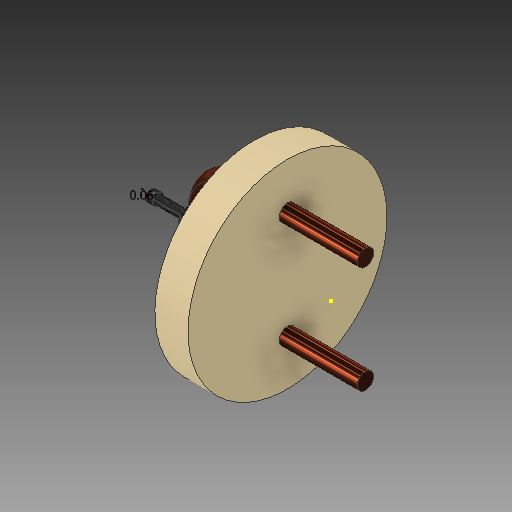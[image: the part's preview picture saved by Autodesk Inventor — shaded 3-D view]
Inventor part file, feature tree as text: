
AUTODESK INVENTOR PART (.ipt)
format: ipt  version: 2017.3 (Build 213256000, 256)  size: 282,112 bytes
history: native  units: mm
features: sketch x23, extrude x12, plane x8, other x6, sweep x2, move_body x1, loft x1
ambient origin geometry x8: Origin, YZ Plane, XZ Plane, XY Plane, X Axis, Y Axis, Z Axis, Center Point
bodies: Solid1 (feature_tree)
feature tree (53):
  extrude  "Extrusion1"  Depth=2.0mm TaperAngle=0.0deg
  sketch  "Sketch2"  dims[d3=1.0mm d4=7.45mm]
  move_body  "Move Body1"
  extrude  "Extrusion2"  Depth=1.0mm
  plane  "Work Plane2"
  sketch  "Sketch3"  dims[d5=1.0mm d6=1.0mm]
  sketch  "Sketch4"  dims[d7=-4.7mm d8=0.0mm d9=0.0mm d10=7.7mm d11=0.0mm]
  sketch  "Sketch5"  dims[d13=3.5mm d14=1.0mm]
  sweep  "Sweep1"
  sketch  "Sketch7"  dims[d21=90.0deg d22=0.5mm d23=-0.5mm d24=0.2mm d25=0.0mm]
  sketch  "Sketch8"  dims[d26=0.1mm d27=0.0mm d28=0.2mm d29=0.0mm]
  sketch  "Sketch9"  dims[d30=0.1mm d31=0.0mm d33=0.25mm]
  plane  "Work Plane3"
  sweep  "Sweep2"
  other  "Work Axis1"
  other  "Work Point1"
  other  "Work Point2"
  other  "Work Point3"
  plane  "Work Plane4"
  plane  "Work Plane5"
  plane  "Work Plane6"
  extrude  "Extrusion3"  Depth=1.0mm
  extrude  "Extrusion4"  TaperAngle=0.0deg  [1 undecoded]
  extrude  "Extrusion5"  Depth=0.2mm TaperAngle=0.0deg
  extrude  "Extrusion6"  Depth=0.2mm TaperAngle=0.0deg
  sketch  "Sketch14"  dims[d47=0.7mm d48=0.4mm d49=0.0mm]
  sketch  "Sketch15"  dims[d50=0.277mm d51=-0.077mm d52=0.06mm]
  extrude  "Extrusion7"  Depth=0.25mm
  extrude  "Extrusion8"  Depth=0.25mm
  extrude  "Extrusion9"  Depth=0.6mm TaperAngle=0.0deg
  plane  "Work Plane7"
  extrude  "Extrusion10"  Depth=1.064mm TaperAngle=0.0deg
  extrude  "Extrusion11"  Depth=1.8mm TaperAngle=0.0deg
  extrude  "Extrusion12"  Depth=0.4mm TaperAngle=0.0deg
  plane  "Work Plane9"
  sketch  "Sketch22"
  loft  "Loft1"
  sketch  "Sketch1"  dims[d0=12.0mm d1=2.0mm d2=0.0mm]
  sketch  "Sketch6"  dims[d16=0.0mm d17=0.0mm d19=0.0mm d20=0.0mm]
  other  "Work Axis2"
  sketch  "Sketch10"  dims[d34=0.6mm d35=0.0mm d36=0.25mm]
  sketch  "Sketch11"  dims[d37=0.6mm d38=0.0mm d39=0.02mm d40=0.0mm]
  sketch  "Sketch12"  dims[d41=1.1mm d42=1.064mm d43=0.0mm]
  sketch  "Sketch13"  dims[d44=0.55mm d45=1.8mm d46=0.0mm]
  sketch  "Sketch16"  dims[d53=0.0mm d54=90.0deg]
  sketch  "Sketch17"  dims[d55=0.0mm d56=90.0deg]
  sketch  "Sketch18"
  sketch  "Sketch19"
  sketch  "Sketch20"
  sketch  "Sketch21"
  plane  "Work Plane8"
  sketch  "Sketch23"
  other  "Edges1"
note: 1 required parameter value undecoded (feature->parameter linkage not recoverable at this tier; creation-order binding heuristic only, values carry confidence <= 0.55)
